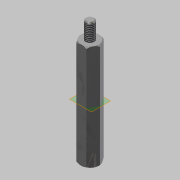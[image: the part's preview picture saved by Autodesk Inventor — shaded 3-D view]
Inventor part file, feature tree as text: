
AUTODESK INVENTOR PART (.ipt)
format: ipt  version: 2014 (Build 180170000, 170)  size: 130,560 bytes
history: native  units: mm
features: sketch x4, extrude x3, chamfer x2, hole x1, plane x1, mirror x1, thread x1
ambient origin geometry x8: Origin, YZ Plane, XZ Plane, XY Plane, X Axis, Y Axis, Z Axis, Center Point
bodies: Solid1 (feature_tree)
feature tree (13):
  extrude  "Extrusion1"  Depth=30.0mm TaperAngle=0.0deg
  hole  "Hole1"  [1 undecoded]
  chamfer  "Chamfer2"  Distance=1.0mm
  extrude  "Extrusion3"  Depth=10.0mm TaperAngle=0.0deg
  plane  "Work Plane1"
  mirror  "Mirror2"
  extrude  "Extrusion4"  [1 undecoded]
  thread  "Thread2"  [1 undecoded]
  chamfer  "Chamfer4"  [1 undecoded]
  sketch  "Sketch1"  dims[d0=5.0mm d1=30.0mm d2=0.0mm]
  sketch  "Sketch3"  dims[d11=2.459mm d12=10.0mm d13=4.0mm d14=2.0mm d15=90.0deg d16=8.0mm d17=20.594885mm d18=0.5mm d19=2.0mm d20=45.0deg d21=1.0mm d22=-7.853982mm]
  sketch  "Sketch4"  dims[d26=5.0mm d27=25.0mm d28=0.0mm d29=0.0mm d30=10.0mm d31=0.0mm]
  sketch  "Sketch5"  dims[d32=0.3mm d33=2.0mm d34=45.0deg]
note: 4 required parameter values undecoded (feature->parameter linkage not recoverable at this tier; creation-order binding heuristic only, values carry confidence <= 0.55)
